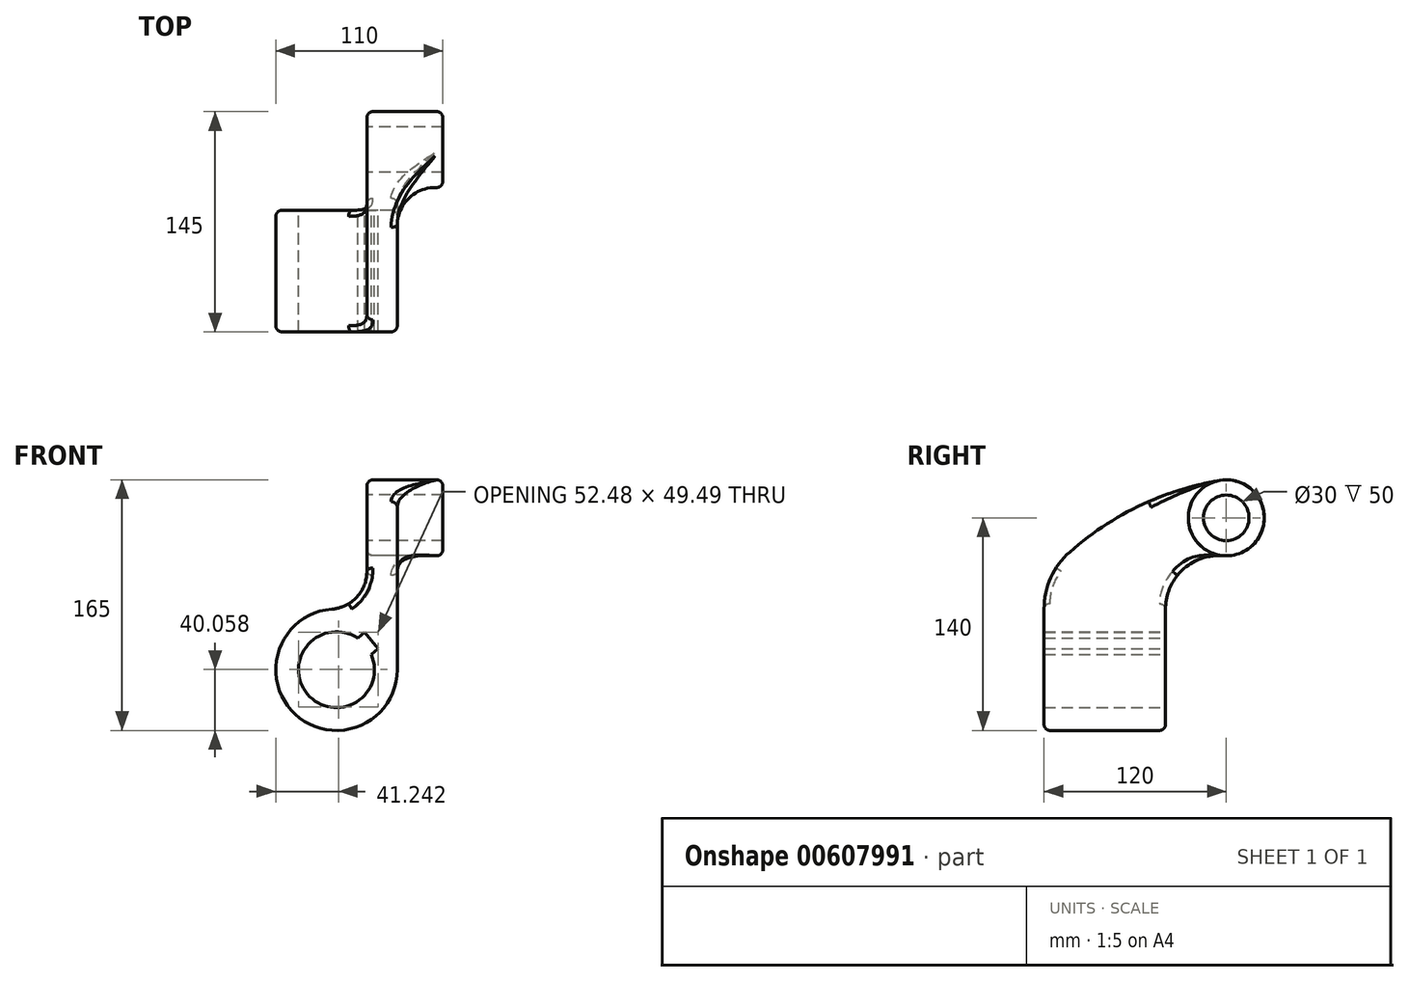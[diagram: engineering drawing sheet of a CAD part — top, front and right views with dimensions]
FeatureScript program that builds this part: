
annotation { "Feature Type Name" : "Feature", "Feature Type Description" : "" }
export const myFeature = defineFeature(function(context is Context, id is Id, definition is map)
    precondition{}
    {
        {
            var Q0;
            Q0=qCreatedBy(makeId("Right.planeOp"),FACE);
            var sketch = newSketch(context, id + "F0", { "sketchPlane" : qUnion([Q0])});
            skLineSegment(sketch, "E0", {"start": v(0, 0) * mm, "end": v(-80, 0) * mm});
            skLineSegment(sketch, "E1", {"start": v(-80, 0) * mm, "end": v(-80, 40) * mm});
            skLineSegment(sketch, "E2", {"start": v(-80, 40) * mm, "end": v(0, 40) * mm});
            skLineSegment(sketch, "E3", {"start": v(0, 40) * mm, "end": v(0, 0) * mm});
            skCircle(sketch, "E4", {"center": v(40, 100) * mm, "radius": 15 * mm});
            skCircle(sketch, "E5", {"center": v(40, 100) * mm, "radius": 25 * mm});
            skArc(sketch, "E6", {"start": v(38, 75.08) * mm, "mid": v(11.32, 65.86) * mm, "end": v(0, 40) * mm});
            skArc(sketch, "E7", {"start": v(-63.05, 77.52) * mm, "mid": v(-75.57, 60.58) * mm, "end": v(-80, 40) * mm});
            skArc(sketch, "E8", {"start": v(35.84, 124.65) * mm, "mid": v(-16.9, 107.99) * mm, "end": v(-63.05, 77.52) * mm});
            skSolve(sketch);
        }
        {
            var Q0;
            Q0=makeQuery(id+"F0.imprint","IMPRINT",FACE,{"disambiguationData":[TD([[makeQuery(id+"F0.imprint","IMPRINT",EDGE,{"derivedFrom":sQuery(id+"F0.wireOp",EDGE,"E4")}),-1.0]])]});
            extrude(context, id + "F1", {"entities" : qUnion([Q0]), "depth" : 50 * mm, "offsetDistance" : 25 * mm});
        }
        {
            var Q0;
            Q0=qSketchRegion(id+"F0",true);
            extrude(context, id + "F2", {"entities" : qUnion([Q0]), "operationType" : NewBodyOperationType.ADD, "depth" : 20 * mm, "offsetDistance" : 25 * mm});
        }
        {
            var Q0;
            Q0=qCreatedBy(makeId("Front.planeOp"),FACE);
            var sketch = newSketch(context, id + "F3", { "sketchPlane" : qUnion([Q0])});
            skLineSegment(sketch, "E9", {"start": v(0, 0) * mm, "end": v(-20, 0) * mm, "construction": true});
            skCircle(sketch, "E10", {"center": v(-20, 0) * mm, "radius": 40 * mm});
            skCircle(sketch, "E11", {"center": v(-20, 0) * mm, "radius": 25 * mm});
            skLineSegment(sketch, "E12", {"start": v(-20, 0) * mm, "end": v(25.96, 38.57) * mm, "construction": true});
            skLineSegment(sketch, "E13", {"start": v(-0.85, 16.07) * mm, "end": v(2.98, 19.28) * mm});
            skLineSegment(sketch, "E14", {"start": v(2.98, 19.28) * mm, "end": v(7.48, 13.92) * mm});
            skLineSegment(sketch, "E15", {"start": v(7.48, 13.92) * mm, "end": v(2.88, 10.06) * mm});
            skLineSegment(sketch, "E16", {"start": v(2.98, 19.28) * mm, "end": v(-1.52, 24.65) * mm});
            skLineSegment(sketch, "E17", {"start": v(-1.52, 24.65) * mm, "end": v(-6.11, 20.79) * mm});
            skSolve(sketch);
        }
        {
            var Q0;
            Q0=makeQuery(id+"F3.imprint","IMPRINT",FACE,{"disambiguationData":[TD([[makeQuery(id+"F3.imprint","IMPRINT",EDGE,{"derivedFrom":sQuery(id+"F3.wireOp",EDGE,"E10")}),1.0]])]});
            extrude(context, id + "F4", {"entities" : qUnion([Q0]), "operationType" : NewBodyOperationType.ADD, "depth" : 80 * mm, "offsetDistance" : 25 * mm});
        }
        {
            var Q0;
            Q0=makeQuery(id+"F3.imprint","IMPRINT",FACE,{"disambiguationData":[TD([[makeQuery(id+"F3.imprint","IMPRINT",EDGE,{"derivedFrom":sQuery(id+"F3.wireOp",EDGE,"E11")}),1.0]])]});
            extrude(context, id + "F5", {"entities" : qUnion([Q0]), "operationType" : NewBodyOperationType.REMOVE, "depth" : 80 * mm, "offsetDistance" : 25 * mm});
        }
        {
            var Q0;
            {var subQ0=sQuery(id+"F0.wireOp",EDGE,"E5");Q0=makeQuery(id+"F2.boolean.opBoolean","INTERSECT",EDGE,{"derivedFrom":[makeQuery(id+"F1.opExtrude","SWEPT_FACE",FACE,{"disambiguationData":[OSD([subQ0])]}),makeQuery(id+"F2.opExtrude","CAP_FACE",FACE,{"disambiguationData":[OSD([sQuery(id+"F0.wireOp",EDGE,"E0"),sQuery(id+"F0.wireOp",EDGE,"E1"),sQuery(id+"F0.wireOp",EDGE,"E3"),sQuery(id+"F0.wireOp",EDGE,"E4"),subQ0,sQuery(id+"F0.wireOp",EDGE,"E6"),sQuery(id+"F0.wireOp",EDGE,"E7"),sQuery(id+"F0.wireOp",EDGE,"E8")])],"isStart":false})]});}
            fillet(context, id + "F6", {"entities" : qUnion([Q0]), "radius" : 25 * mm, "tangentPropagation" : true, "allowEdgeOverflow" : false});
        }
        {
            var Q0;
            {var subQ0=sQuery(id+"F3.wireOp",EDGE,"E13");Q0=makeQuery(id+"F3.imprint","IMPRINT",FACE,{"disambiguationData":[TD([[makeQuery(id+"F3.imprint","IMPRINT",EDGE,{"derivedFrom":subQ0}),-1.0]])]});}
            var Q1;
            {var subQ0=sQuery(id+"F3.wireOp",EDGE,"E13");Q1=makeQuery(id+"F3.imprint","IMPRINT",FACE,{"disambiguationData":[TD([[makeQuery(id+"F3.imprint","IMPRINT",EDGE,{"derivedFrom":subQ0}),1.0]])]});}
            extrude(context, id + "F7", {"entities" : qUnion([Q0, Q1]), "operationType" : NewBodyOperationType.REMOVE, "depth" : 80 * mm, "offsetDistance" : 25 * mm});
        }
        {
            var Q0;
            {var subQ0=sQuery(id+"F0.wireOp",EDGE,"E5");var subQ1=sQuery(id+"F0.wireOp",EDGE,"E4");Q0=makeQuery(id+"F4.boolean.opBoolean","INTERSECT",EDGE,{"derivedFrom":[makeQuery(id+"F2.boolean.opBoolean","MERGE",FACE,{"derivedFrom":[makeQuery(id+"F1.opExtrude","CAP_FACE",FACE,{"disambiguationData":[OSD([subQ1,subQ0])],"isStart":true}),makeQuery(id+"F2.opExtrude","CAP_FACE",FACE,{"disambiguationData":[OSD([sQuery(id+"F0.wireOp",EDGE,"E0"),sQuery(id+"F0.wireOp",EDGE,"E1"),sQuery(id+"F0.wireOp",EDGE,"E3"),subQ1,subQ0,sQuery(id+"F0.wireOp",EDGE,"E6"),sQuery(id+"F0.wireOp",EDGE,"E7"),sQuery(id+"F0.wireOp",EDGE,"E8")])],"isStart":true})]}),makeQuery(id+"F4.opExtrude","SWEPT_FACE",FACE,{"disambiguationData":[OSD([sQuery(id+"F3.wireOp",EDGE,"E10")])]})]});}
            fillet(context, id + "F8", {"entities" : qUnion([Q0]), "radius" : 25 * mm, "tangentPropagation" : true, "allowEdgeOverflow" : false});
        }
        {
            var Q0;
            Q0=makeQuery(id+"F4.opExtrude","CAP_EDGE",EDGE,{"disambiguationData":[OSD([sQuery(id+"F3.wireOp",EDGE,"E10")])],"isStart":false});
            var Q1;
            Q1=makeQuery(id+"F1.opExtrude","CAP_EDGE",EDGE,{"disambiguationData":[OSD([sQuery(id+"F0.wireOp",EDGE,"E5")])],"isStart":false});
            fillet(context, id + "F9", {"entities" : qUnion([Q0, Q1]), "radius" : 4 * mm, "tangentPropagation" : true, "allowEdgeOverflow" : false});
        }
    });
